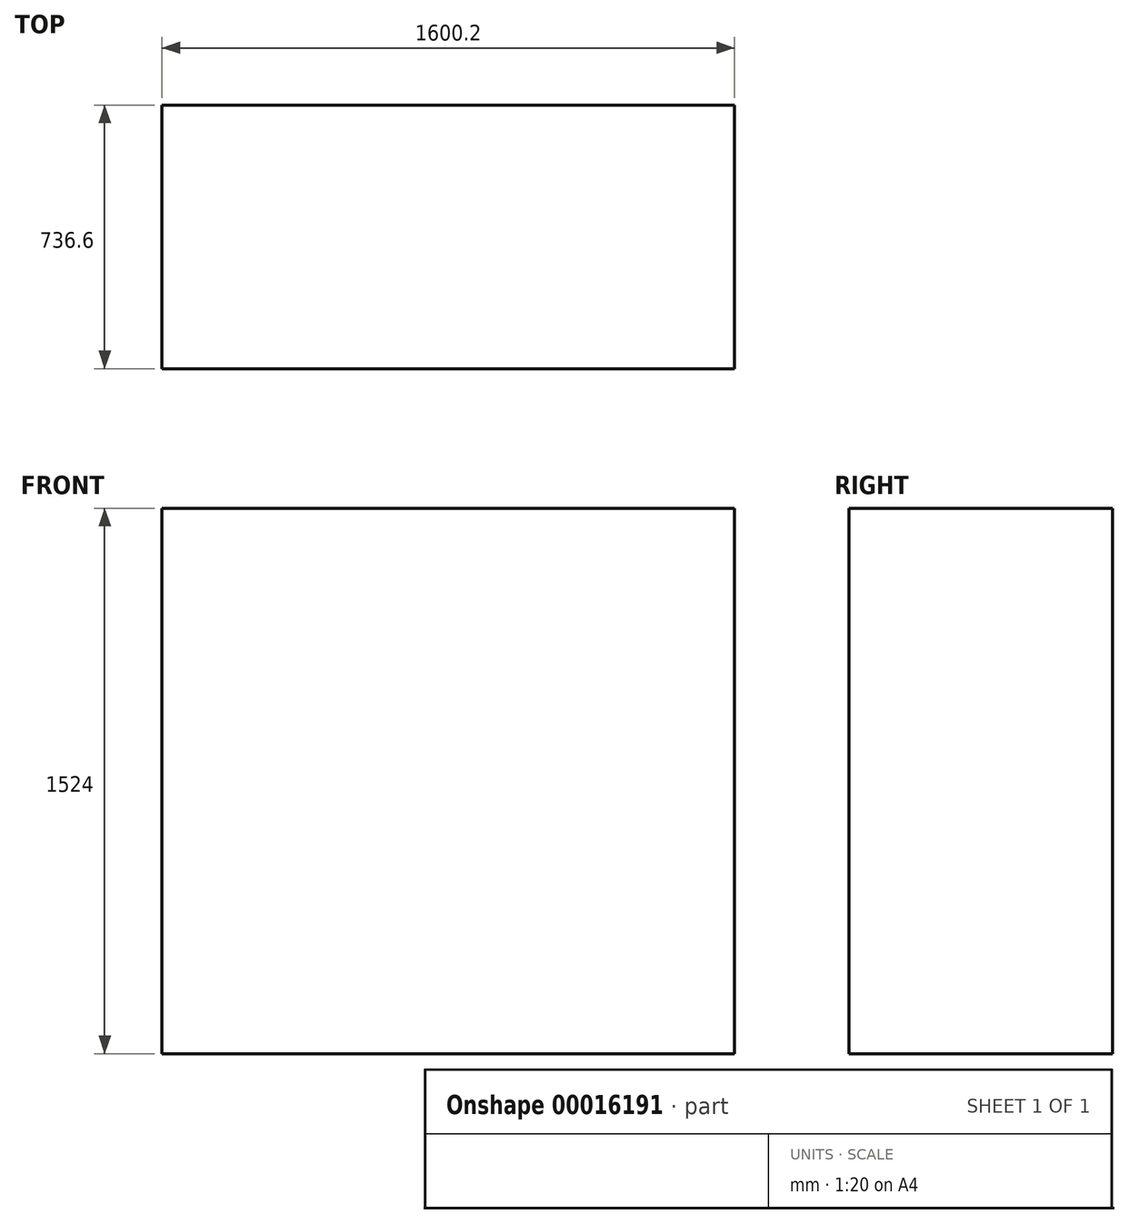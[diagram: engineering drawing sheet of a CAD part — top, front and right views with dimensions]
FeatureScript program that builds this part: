
annotation { "Feature Type Name" : "Feature", "Feature Type Description" : "" }
export const myFeature = defineFeature(function(context is Context, id is Id, definition is map)
    precondition{}
    {
        {
            var Q0;
            Q0=qCreatedBy(makeId("Top.planeOp"),FACE);
            var sketch = newSketch(context, id + "F0", { "sketchPlane" : qUnion([Q0])});
            skLineSegment(sketch, "E0.rect.bottom", {"start": v(800.1, 368.3) * mm, "end": v(-800.1, 368.3) * mm});
            skLineSegment(sketch, "E0.rect.top", {"start": v(800.1, -368.3) * mm, "end": v(-800.1, -368.3) * mm});
            skLineSegment(sketch, "E0.rect.left", {"start": v(800.1, 368.3) * mm, "end": v(800.1, -368.3) * mm});
            skLineSegment(sketch, "E0.rect.right", {"start": v(-800.1, 368.3) * mm, "end": v(-800.1, -368.3) * mm});
            skPoint(sketch, "E0.rect.middle", {"position": v(0, 0) * mm});
            skSolve(sketch);
        }
        {
            var Q0;
            Q0 = qSketchRegion(id + "F0", true);
            extrude(context, id + "F1", {"entities" : qUnion([Q0]), "depth" : 5 * 304.8 * mm});
        }
    });
